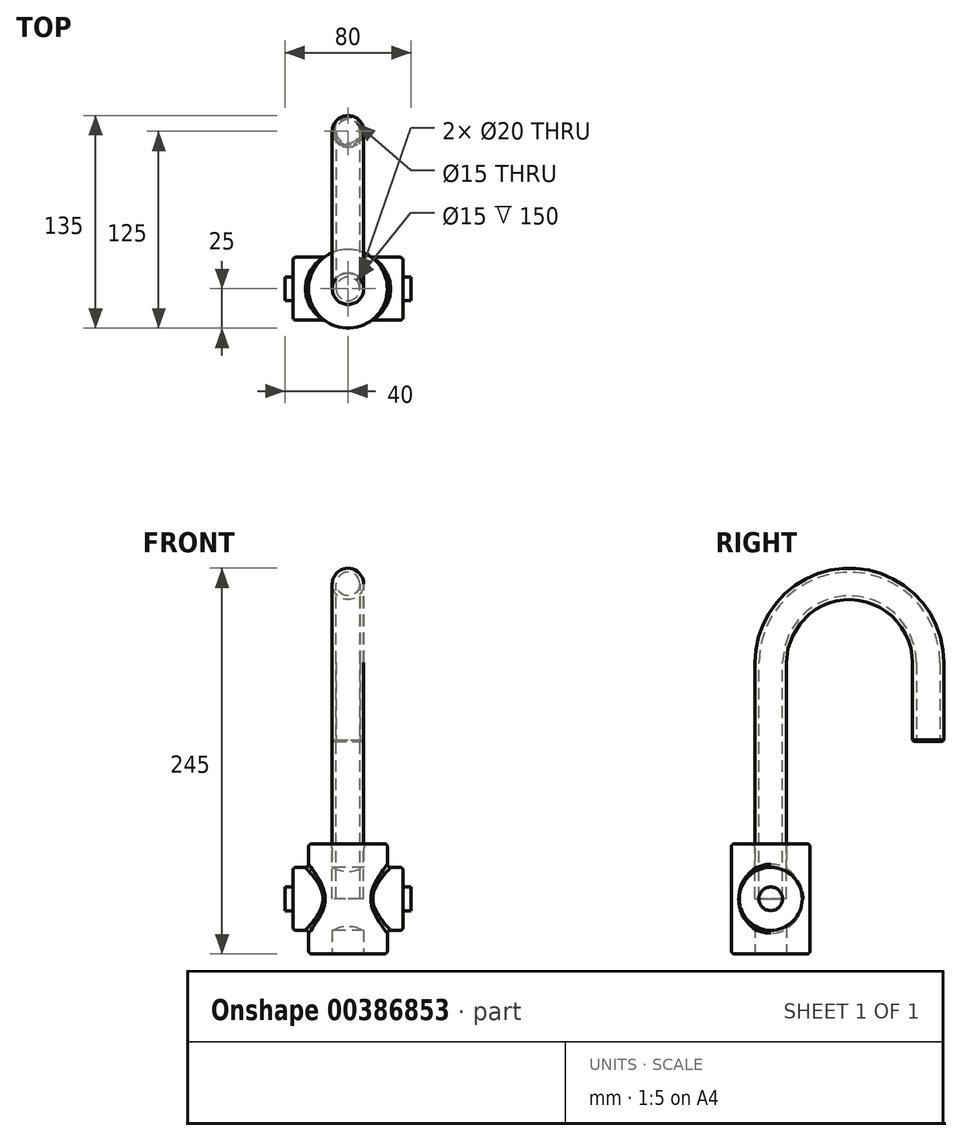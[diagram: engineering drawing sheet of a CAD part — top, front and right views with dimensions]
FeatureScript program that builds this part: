
annotation { "Feature Type Name" : "Feature", "Feature Type Description" : "" }
export const myFeature = defineFeature(function(context is Context, id is Id, definition is map)
    precondition{}
    {
        {
            var Q0;
            Q0=qCreatedBy(makeId("Top.planeOp"),FACE);
            var sketch = newSketch(context, id + "F0", { "sketchPlane" : qUnion([Q0])});
            skCircle(sketch, "E0", {"center": v(0, 0) * mm, "radius": 25 * mm});
            skCircle(sketch, "E1", {"center": v(0, 0) * mm, "radius": 10 * mm});
            skCircle(sketch, "E2", {"center": v(0, 0) * mm, "radius": 7.5 * mm});
            skSolve(sketch);
        }
        {
            var Q0;
            Q0=qCreatedBy(makeId("Right.planeOp"),FACE);
            var sketch = newSketch(context, id + "F1", { "sketchPlane" : qUnion([Q0])});
            skCircle(sketch, "E3", {"center": v(0, 0) * mm, "radius": 20 * mm});
            skLineSegment(sketch, "E4", {"start": v(0, 0) * mm, "end": v(0, 150) * mm});
            skLineSegment(sketch, "E5", {"start": v(100, 150) * mm, "end": v(100, 100) * mm});
            skArc(sketch, "E6", {"start": v(100, 150) * mm, "mid": v(50, 200) * mm, "end": v(0, 150) * mm});
            skLineSegment(sketch, "E7", {"start": v(0, 0) * mm, "end": v(0, -70) * mm});
            skSolve(sketch);
        }
        {
            var Q0;
            Q0=makeQuery(id+"F0.imprint","IMPRINT",FACE,{"disambiguationData":[TD([[makeQuery(id+"F0.imprint","IMPRINT",EDGE,{"derivedFrom":sQuery(id+"F0.wireOp",EDGE,"E0")}),1.0]])]});
            extrude(context, id + "F2", {"entities" : qUnion([Q0]), "depth" : 70 * mm, "symmetric" : true});
        }
        {
            var Q0;
            Q0 = qSketchRegion(id + "F1", true);
            extrude(context, id + "F3", {"entities" : qUnion([Q0]), "operationType" : NewBodyOperationType.ADD, "depth" : 70 * mm, "symmetric" : true});
        }
        {
            var Q0;
            Q0=makeQuery(id+"F3.boolean.opBoolean","INTERSECT",EDGE,{"disambiguationData":[OD(1.0)],"derivedFrom":[makeQuery(id+"F2.opExtrude","SWEPT_FACE",FACE,{"disambiguationData":[OSD([sQuery(id+"F0.wireOp",EDGE,"E0")])]}),makeQuery(id+"F3.opExtrude","SWEPT_FACE",FACE,{"disambiguationData":[OSD([sQuery(id+"F1.wireOp",EDGE,"E3")])]})]});
            var Q1;
            Q1=makeQuery(id+"F3.boolean.opBoolean","INTERSECT",EDGE,{"disambiguationData":[OD(0.0)],"derivedFrom":[makeQuery(id+"F2.opExtrude","SWEPT_FACE",FACE,{"disambiguationData":[OSD([sQuery(id+"F0.wireOp",EDGE,"E0")])]}),makeQuery(id+"F3.opExtrude","SWEPT_FACE",FACE,{"disambiguationData":[OSD([sQuery(id+"F1.wireOp",EDGE,"E3")])]})]});
            var Q2;
            Q2=makeQuery(id+"F3.opExtrude","CAP_EDGE",EDGE,{"disambiguationData":[OSD([sQuery(id+"F1.wireOp",EDGE,"E3")])],"isStart":false});
            var Q3;
            Q3=makeQuery(id+"F2.opExtrude","CAP_EDGE",EDGE,{"disambiguationData":[OSD([sQuery(id+"F0.wireOp",EDGE,"E0")])],"isStart":false});
            var Q4;
            Q4=makeQuery(id+"F3.opExtrude","CAP_EDGE",EDGE,{"disambiguationData":[OSD([sQuery(id+"F1.wireOp",EDGE,"E3")])],"isStart":true});
            var Q5;
            Q5=makeQuery(id+"F2.opExtrude","CAP_EDGE",EDGE,{"disambiguationData":[OSD([sQuery(id+"F0.wireOp",EDGE,"E0")])],"isStart":true});
            fillet(context, id + "F4", {"entities" : qUnion([Q0, Q1, Q2, Q3, Q4, Q5]), "radius" : 2 * mm, "tangentPropagation" : true, "allowEdgeOverflow" : false});
        }
        {
            var Q0;
            Q0=makeQuery(id+"F0.imprint","IMPRINT",FACE,{"disambiguationData":[TD([[makeQuery(id+"F0.imprint","IMPRINT",EDGE,{"derivedFrom":sQuery(id+"F0.wireOp",EDGE,"E1")}),1.0]])]});
            var Q1;
            Q1=sQuery(id+"F1.wireOp",EDGE,"E4");
            var Q2;
            Q2=sQuery(id+"F1.wireOp",EDGE,"E6");
            var Q3;
            Q3=sQuery(id+"F1.wireOp",EDGE,"E5");
            sweep(context, id + "F5", {"profiles" : qUnion([Q0]), "path" : qUnion([Q1, Q2, Q3])});
        }
        {
            var Q0;
            Q0=makeQuery(id+"F2.opExtrude","CAP_EDGE",EDGE,{"disambiguationData":[OSD([sQuery(id+"F0.wireOp",EDGE,"E1")])],"isStart":false});
            fillet(context, id + "F6", {"entities" : qUnion([Q0]), "radius" : 3 * mm, "tangentPropagation" : true, "defaultsChanged" : true, "vertexSettings" : [], "allowEdgeOverflow" : false});
        }
        {
            var Q0;
            Q0=makeQuery(id+"F5.opSweep","CAP_EDGE",EDGE,{"disambiguationData":[OSD([sQuery(id+"F0.wireOp",EDGE,"E1"),sQuery(id+"F1.wireOp",VERTEX,"E5.end")])],"isStart":false});
            var Q1;
            Q1=makeQuery(id+"F5.opSweep","CAP_EDGE",EDGE,{"disambiguationData":[OSD([sQuery(id+"F0.wireOp",EDGE,"E2"),sQuery(id+"F1.wireOp",VERTEX,"E5.end")])],"isStart":false});
            chamfer(context, id + "F7", {"entities" : qUnion([Q0, Q1]), "width" : 1 * mm, "tangentPropagation" : true});
        }
        {
            var Q0;
            Q0=makeQuery(id+"F3.opExtrude","CAP_FACE",FACE,{"disambiguationData":[OSD([sQuery(id+"F1.wireOp",EDGE,"E3")])],"isStart":true});
            var sketch = newSketch(context, id + "F8", { "sketchPlane" : qUnion([Q0])});
            skCircle(sketch, "E8", {"center": v(0, 0) * mm, "radius": 7.5 * mm});
            skSolve(sketch);
        }
        {
            var Q0;
            Q0=makeQuery(id+"F3.opExtrude","CAP_FACE",FACE,{"disambiguationData":[OSD([sQuery(id+"F1.wireOp",EDGE,"E3")])],"isStart":false});
            var sketch = newSketch(context, id + "F9", { "sketchPlane" : qUnion([Q0])});
            skCircle(sketch, "E9", {"center": v(0, 0) * mm, "radius": 7.5 * mm});
            skSolve(sketch);
        }
        {
            var Q0;
            Q0=makeQuery(id+"F9.imprint","IMPRINT",FACE,{"disambiguationData":[TD([[makeQuery(id+"F9.imprint","IMPRINT",EDGE,{"derivedFrom":sQuery(id+"F9.wireOp",EDGE,"E9")}),1.0]])]});
            var Q1;
            Q1=makeQuery(id+"F8.imprint","IMPRINT",FACE,{"disambiguationData":[TD([[makeQuery(id+"F8.imprint","IMPRINT",EDGE,{"derivedFrom":sQuery(id+"F8.wireOp",EDGE,"E8")}),1.0]])]});
            extrude(context, id + "F10", {"entities" : qUnion([Q0, Q1]), "operationType" : NewBodyOperationType.ADD, "depth" : 10 * mm, "symmetric" : true});
        }
    });
